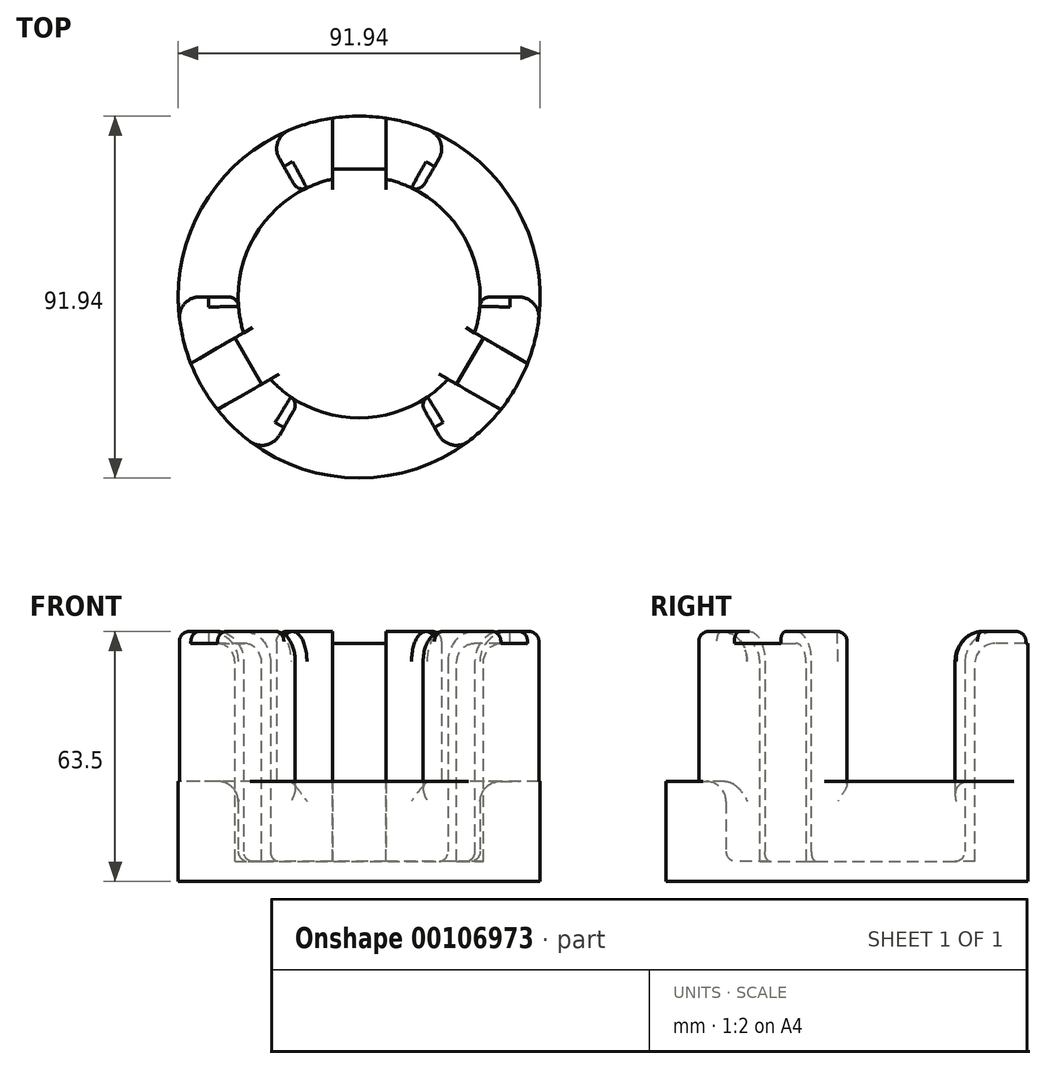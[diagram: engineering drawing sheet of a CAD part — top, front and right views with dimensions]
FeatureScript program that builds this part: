
annotation { "Feature Type Name" : "Feature", "Feature Type Description" : "" }
export const myFeature = defineFeature(function(context is Context, id is Id, definition is map)
    precondition{}
    {
        {
            var Q0;
            Q0=qCreatedBy(makeId("Front.planeOp"),FACE);
            var sketch = newSketch(context, id + "F0", { "sketchPlane" : qUnion([Q0])});
            skLineSegment(sketch, "E0", {"start": v(0, 0) * mm, "end": v(45.97, 0) * mm});
            skLineSegment(sketch, "E1", {"start": v(45.97, 0) * mm, "end": v(45.97, 63.5) * mm});
            skLineSegment(sketch, "E2", {"start": v(45.97, 63.5) * mm, "end": v(38.35, 63.5) * mm});
            skLineSegment(sketch, "E3", {"start": v(30.73, 55.88) * mm, "end": v(30.73, 5.08) * mm});
            skLineSegment(sketch, "E4", {"start": v(30.73, 5.08) * mm, "end": v(0, 5.08) * mm});
            skLineSegment(sketch, "E5", {"start": v(0, 5.08) * mm, "end": v(0, 0) * mm});
            skPoint(sketch, "E6.visualSharp", {"position": v(30.73, 63.5) * mm});
            skArc(sketch, "E6.filletArc", {"start": v(38.35, 63.5) * mm, "mid": v(32.97, 61.27) * mm, "end": v(30.73, 55.88) * mm});
            skLineSegment(sketch, "E7", {"start": v(0, 0) * mm, "end": v(0, 66.33) * mm, "construction": true});
            skSolve(sketch);
        }
        {
            var Q0;
            Q0=makeQuery(id+"F0.imprint","IMPRINT",FACE,{"disambiguationData":[TD([[makeQuery(id+"F0.imprint","IMPRINT",EDGE,{"derivedFrom":sQuery(id+"F0.wireOp",EDGE,"E0")}),1.0]])]});
            var Q1;
            Q1=sQuery(id+"F0.wireOp",EDGE,"E7");
            revolve(context, id + "F1", {"entities" : qUnion([Q0]), "axis" : qUnion([Q1]), "revolveType" : RevolveType.FULL});
        }
        {
            var Q0;
            Q0=makeQuery(id+"F1.opRevolve","SWEPT_FACE",FACE,{"disambiguationData":[OSD([sQuery(id+"F0.wireOp",EDGE,"E2")])]});
            var sketch = newSketch(context, id + "F2", { "sketchPlane" : qUnion([Q0])});
            skLineSegment(sketch, "E8.bottom", {"start": v(6.8, 32.51) * mm, "end": v(-6.8, 32.51) * mm});
            skLineSegment(sketch, "E8.top", {"start": v(6.8, 28.96) * mm, "end": v(-6.8, 28.96) * mm});
            skLineSegment(sketch, "E8.left", {"start": v(6.8, 32.51) * mm, "end": v(6.8, 28.96) * mm});
            skLineSegment(sketch, "E8.right", {"start": v(-6.8, 32.51) * mm, "end": v(-6.8, 28.96) * mm});
            skPoint(sketch, "E8.middle", {"position": v(0, 30.73) * mm});
            skLineSegment(sketch, "E9.1.0", {"start": v(-31.55, -10.37) * mm, "end": v(-28.47, -8.6) * mm});
            skLineSegment(sketch, "E9.1.1", {"start": v(-28.47, -8.6) * mm, "end": v(-21.68, -20.36) * mm});
            skLineSegment(sketch, "E9.1.2", {"start": v(-24.76, -22.14) * mm, "end": v(-21.68, -20.36) * mm});
            skLineSegment(sketch, "E9.1.3", {"start": v(-31.55, -10.37) * mm, "end": v(-24.76, -22.14) * mm});
            skLineSegment(sketch, "E9.2.0", {"start": v(24.76, -22.14) * mm, "end": v(21.68, -20.36) * mm});
            skLineSegment(sketch, "E9.2.1", {"start": v(21.68, -20.36) * mm, "end": v(28.47, -8.6) * mm});
            skLineSegment(sketch, "E9.2.2", {"start": v(31.55, -10.37) * mm, "end": v(28.47, -8.6) * mm});
            skLineSegment(sketch, "E9.2.3", {"start": v(24.76, -22.14) * mm, "end": v(31.55, -10.37) * mm});
            skPoint(sketch, "E9.center", {"position": v(0, 0) * mm});
            skSolve(sketch);
        }
        {
            var Q0;
            Q0 = qSketchRegion(id + "F2", true);
            extrude(context, id + "F3", {"entities" : qUnion([Q0]), "operationType" : NewBodyOperationType.REMOVE, "oppositeDirection" : true, "depth" : 58.42 * mm});
        }
        {
            var Q0;
            Q0=makeQuery(id+"F1.opRevolve","SWEPT_FACE",FACE,{"disambiguationData":[OSD([sQuery(id+"F0.wireOp",EDGE,"E2")])]});
            var sketch = newSketch(context, id + "F4", { "sketchPlane" : qUnion([Q0])});
            skLineSegment(sketch, "E10.bottom", {"start": v(-6.8, 52.9) * mm, "end": v(6.8, 52.9) * mm});
            skLineSegment(sketch, "E10.top", {"start": v(-6.8, 28.96) * mm, "end": v(6.8, 28.96) * mm});
            skLineSegment(sketch, "E10.left", {"start": v(-6.8, 52.9) * mm, "end": v(-6.8, 28.96) * mm});
            skLineSegment(sketch, "E10.right", {"start": v(6.8, 52.9) * mm, "end": v(6.8, 28.96) * mm});
            skLineSegment(sketch, "E11.1.0", {"start": v(-42.41, -32.33) * mm, "end": v(-49.2, -20.57) * mm});
            skLineSegment(sketch, "E11.1.1", {"start": v(-42.41, -32.33) * mm, "end": v(-21.68, -20.36) * mm});
            skLineSegment(sketch, "E11.1.2", {"start": v(-49.2, -20.57) * mm, "end": v(-28.47, -8.6) * mm});
            skLineSegment(sketch, "E11.1.3", {"start": v(-21.68, -20.36) * mm, "end": v(-28.47, -8.6) * mm});
            skLineSegment(sketch, "E11.2.0", {"start": v(49.2, -20.57) * mm, "end": v(42.41, -32.33) * mm});
            skLineSegment(sketch, "E11.2.1", {"start": v(49.2, -20.57) * mm, "end": v(28.47, -8.6) * mm});
            skLineSegment(sketch, "E11.2.2", {"start": v(42.41, -32.33) * mm, "end": v(21.68, -20.36) * mm});
            skLineSegment(sketch, "E11.2.3", {"start": v(28.47, -8.6) * mm, "end": v(21.68, -20.36) * mm});
            skPoint(sketch, "E11.center", {"position": v(0, 0) * mm});
            skSolve(sketch);
        }
        {
            var Q0;
            Q0 = qSketchRegion(id + "F4", true);
            extrude(context, id + "F5", {"entities" : qUnion([Q0]), "operationType" : NewBodyOperationType.REMOVE, "oppositeDirection" : true, "depth" : 3.05 * mm});
        }
        {
            var Q0;
            Q0=makeQuery(id+"F5.boolean.opBoolean","INTERSECT",EDGE,{"derivedFrom":[makeQuery(id+"F3.boolean.opBoolean","COPY",FACE,{"derivedFrom":makeQuery(id+"F3.opExtrude","SWEPT_FACE",FACE,{"disambiguationData":[OSD([sQuery(id+"F2.wireOp",EDGE,"E9.1.3")])]})}),makeQuery(id+"F5.opExtrude","CAP_FACE",FACE,{"disambiguationData":[OSD([sQuery(id+"F4.wireOp",EDGE,"E11.1.0"),sQuery(id+"F4.wireOp",EDGE,"E11.1.1"),sQuery(id+"F4.wireOp",EDGE,"E11.1.2"),sQuery(id+"F4.wireOp",EDGE,"E11.1.3")])],"isStart":false})]});
            var Q1;
            Q1=makeQuery(id+"F5.boolean.opBoolean","INTERSECT",EDGE,{"derivedFrom":[makeQuery(id+"F3.boolean.opBoolean","COPY",FACE,{"derivedFrom":makeQuery(id+"F3.opExtrude","SWEPT_FACE",FACE,{"disambiguationData":[OSD([sQuery(id+"F2.wireOp",EDGE,"E8.bottom")])]})}),makeQuery(id+"F5.opExtrude","CAP_FACE",FACE,{"disambiguationData":[OSD([sQuery(id+"F4.wireOp",EDGE,"E10.bottom"),sQuery(id+"F4.wireOp",EDGE,"E10.top"),sQuery(id+"F4.wireOp",EDGE,"E10.left"),sQuery(id+"F4.wireOp",EDGE,"E10.right")])],"isStart":false})]});
            var Q2;
            Q2=makeQuery(id+"F5.boolean.opBoolean","INTERSECT",EDGE,{"derivedFrom":[makeQuery(id+"F3.boolean.opBoolean","COPY",FACE,{"derivedFrom":makeQuery(id+"F3.opExtrude","SWEPT_FACE",FACE,{"disambiguationData":[OSD([sQuery(id+"F2.wireOp",EDGE,"E9.2.3")])]})}),makeQuery(id+"F5.opExtrude","CAP_FACE",FACE,{"disambiguationData":[OSD([sQuery(id+"F4.wireOp",EDGE,"E11.2.0"),sQuery(id+"F4.wireOp",EDGE,"E11.2.1"),sQuery(id+"F4.wireOp",EDGE,"E11.2.2"),sQuery(id+"F4.wireOp",EDGE,"E11.2.3")])],"isStart":false})]});
            fillet(context, id + "F6", {"entities" : qUnion([Q0, Q1, Q2]), "radius" : 5.08 * mm, "tangentPropagation" : true, "allowEdgeOverflow" : false});
        }
        {
            var Q0;
            {var subQ0=sQuery(id+"F0.wireOp",EDGE,"E2");Q0=makeQuery(id+"F2.imprint","IMPRINT",FACE,{"disambiguationData":[TD([[makeQuery(id+"F2.imprint","IMPRINT",EDGE,{"derivedFrom":makeQuery(id+"F1.opRevolve","SWEPT_EDGE",EDGE,{"disambiguationData":[OSD([sQuery(id+"F0.wireOp",EDGE,"E1"),subQ0])]})}),-1.0]])]});}
            var sketch = newSketch(context, id + "F7", { "sketchPlane" : qUnion([Q0])});
            skLineSegment(sketch, "E12", {"start": v(0, 0) * mm, "end": v(-29.33, -50.8) * mm});
            skLineSegment(sketch, "E13", {"start": v(-29.33, -50.8) * mm, "end": v(0, -50.8) * mm});
            skLineSegment(sketch, "E14", {"start": v(0, -50.8) * mm, "end": v(0, 0) * mm});
            skLineSegment(sketch, "E15.MirrorCS", {"start": v(0, 0) * mm, "end": v(29.33, -50.8) * mm});
            skLineSegment(sketch, "E16.MirrorCS", {"start": v(29.33, -50.8) * mm, "end": v(0, -50.8) * mm});
            skLineSegment(sketch, "E17.1.0", {"start": v(0, 0) * mm, "end": v(58.66, 0) * mm});
            skLineSegment(sketch, "E17.1.1", {"start": v(0, 0) * mm, "end": v(29.33, 50.8) * mm});
            skLineSegment(sketch, "E17.1.2", {"start": v(29.33, 50.8) * mm, "end": v(44, 25.4) * mm});
            skLineSegment(sketch, "E17.2.0", {"start": v(0, 0) * mm, "end": v(-29.33, 50.8) * mm});
            skLineSegment(sketch, "E17.2.1", {"start": v(0, 0) * mm, "end": v(-58.66, 0) * mm});
            skLineSegment(sketch, "E17.2.2", {"start": v(-58.66, 0) * mm, "end": v(-44, 25.4) * mm});
            skPoint(sketch, "E17.center", {"position": v(0, 0) * mm});
            skLineSegment(sketch, "E18.1.1", {"start": v(58.66, 0) * mm, "end": v(44, 25.4) * mm});
            skLineSegment(sketch, "E18.2.1", {"start": v(-29.33, 50.8) * mm, "end": v(-44, 25.4) * mm});
            skSolve(sketch);
        }
        {
            var Q0;
            Q0 = qSketchRegion(id + "F7", true);
            extrude(context, id + "F8", {"entities" : qUnion([Q0]), "operationType" : NewBodyOperationType.REMOVE, "oppositeDirection" : true, "depth" : 38.1 * mm});
        }
        {
            var Q0;
            {var subQ0=sQuery(id+"F2.wireOp",EDGE,"E9.1.2");Q0=makeQuery(id+"F8.boolean.opBoolean","INTERSECT",EDGE,{"derivedFrom":[makeQuery(id+"F3.boolean.opBoolean","SPLIT",FACE,{"disambiguationData":[TD([makeQuery(id+"F3.opExtrude","SWEPT_FACE",FACE,{"disambiguationData":[OSD([subQ0])]})])],"derivedFrom":makeQuery(id+"F1.opRevolve","SWEPT_FACE",FACE,{"disambiguationData":[OSD([sQuery(id+"F0.wireOp",EDGE,"E3")])]})}),makeQuery(id+"F8.opExtrude","CAP_FACE",FACE,{"disambiguationData":[OSD([sQuery(id+"F7.wireOp",EDGE,"E12"),sQuery(id+"F7.wireOp",EDGE,"E13"),sQuery(id+"F7.wireOp",EDGE,"E15.MirrorCS"),sQuery(id+"F7.wireOp",EDGE,"E16.MirrorCS")])],"isStart":false})]});}
            var Q1;
            {var subQ0=sQuery(id+"F2.wireOp",EDGE,"E8.right");Q1=makeQuery(id+"F8.boolean.opBoolean","INTERSECT",EDGE,{"derivedFrom":[makeQuery(id+"F3.boolean.opBoolean","SPLIT",FACE,{"disambiguationData":[TD([makeQuery(id+"F3.opExtrude","SWEPT_FACE",FACE,{"disambiguationData":[OSD([subQ0])]})])],"derivedFrom":makeQuery(id+"F1.opRevolve","SWEPT_FACE",FACE,{"disambiguationData":[OSD([sQuery(id+"F0.wireOp",EDGE,"E3")])]})}),makeQuery(id+"F8.opExtrude","CAP_FACE",FACE,{"disambiguationData":[OSD([sQuery(id+"F7.wireOp",EDGE,"E17.2.0"),sQuery(id+"F7.wireOp",EDGE,"E17.2.1"),sQuery(id+"F7.wireOp",EDGE,"E17.2.2"),sQuery(id+"F7.wireOp",EDGE,"E18.2.1")])],"isStart":false})]});}
            var Q2;
            {var subQ0=sQuery(id+"F2.wireOp",EDGE,"E8.left");Q2=makeQuery(id+"F8.boolean.opBoolean","INTERSECT",EDGE,{"derivedFrom":[makeQuery(id+"F3.boolean.opBoolean","SPLIT",FACE,{"disambiguationData":[TD([makeQuery(id+"F3.opExtrude","SWEPT_FACE",FACE,{"disambiguationData":[OSD([subQ0])]})])],"derivedFrom":makeQuery(id+"F1.opRevolve","SWEPT_FACE",FACE,{"disambiguationData":[OSD([sQuery(id+"F0.wireOp",EDGE,"E3")])]})}),makeQuery(id+"F8.opExtrude","CAP_FACE",FACE,{"disambiguationData":[OSD([sQuery(id+"F7.wireOp",EDGE,"E17.1.0"),sQuery(id+"F7.wireOp",EDGE,"E17.1.1"),sQuery(id+"F7.wireOp",EDGE,"E17.1.2"),sQuery(id+"F7.wireOp",EDGE,"E18.1.1")])],"isStart":false})]});}
            var Q3;
            Q3=makeQuery(id+"F8.boolean.opBoolean","INTERSECT",EDGE,{"derivedFrom":[makeQuery(id+"F1.opRevolve","SWEPT_FACE",FACE,{"disambiguationData":[OSD([sQuery(id+"F0.wireOp",EDGE,"E1")])]}),makeQuery(id+"F8.opExtrude","SWEPT_FACE",FACE,{"disambiguationData":[OSD([sQuery(id+"F7.wireOp",EDGE,"E17.1.0")])]})]});
            var Q4;
            Q4=makeQuery(id+"F8.boolean.opBoolean","INTERSECT",EDGE,{"derivedFrom":[makeQuery(id+"F1.opRevolve","SWEPT_FACE",FACE,{"disambiguationData":[OSD([sQuery(id+"F0.wireOp",EDGE,"E1")])]}),makeQuery(id+"F8.opExtrude","SWEPT_FACE",FACE,{"disambiguationData":[OSD([sQuery(id+"F7.wireOp",EDGE,"E17.1.1")])]})]});
            var Q5;
            Q5=makeQuery(id+"F8.boolean.opBoolean","INTERSECT",EDGE,{"derivedFrom":[makeQuery(id+"F1.opRevolve","SWEPT_FACE",FACE,{"disambiguationData":[OSD([sQuery(id+"F0.wireOp",EDGE,"E1")])]}),makeQuery(id+"F8.opExtrude","SWEPT_FACE",FACE,{"disambiguationData":[OSD([sQuery(id+"F7.wireOp",EDGE,"E17.2.0")])]})]});
            var Q6;
            Q6=makeQuery(id+"F8.boolean.opBoolean","INTERSECT",EDGE,{"derivedFrom":[makeQuery(id+"F1.opRevolve","SWEPT_FACE",FACE,{"disambiguationData":[OSD([sQuery(id+"F0.wireOp",EDGE,"E1")])]}),makeQuery(id+"F8.opExtrude","SWEPT_FACE",FACE,{"disambiguationData":[OSD([sQuery(id+"F7.wireOp",EDGE,"E17.2.1")])]})]});
            var Q7;
            Q7=makeQuery(id+"F8.boolean.opBoolean","INTERSECT",EDGE,{"derivedFrom":[makeQuery(id+"F1.opRevolve","SWEPT_FACE",FACE,{"disambiguationData":[OSD([sQuery(id+"F0.wireOp",EDGE,"E1")])]}),makeQuery(id+"F8.opExtrude","SWEPT_FACE",FACE,{"disambiguationData":[OSD([sQuery(id+"F7.wireOp",EDGE,"E12")])]})]});
            var Q8;
            Q8=makeQuery(id+"F8.boolean.opBoolean","INTERSECT",EDGE,{"derivedFrom":[makeQuery(id+"F1.opRevolve","SWEPT_FACE",FACE,{"disambiguationData":[OSD([sQuery(id+"F0.wireOp",EDGE,"E1")])]}),makeQuery(id+"F8.opExtrude","SWEPT_FACE",FACE,{"disambiguationData":[OSD([sQuery(id+"F7.wireOp",EDGE,"E15.MirrorCS")])]})]});
            fillet(context, id + "F9", {"entities" : qUnion([Q0, Q1, Q2, Q3, Q4, Q5, Q6, Q7, Q8]), "radius" : 5.08 * mm, "tangentPropagation" : true, "allowEdgeOverflow" : false});
        }
        {
            var Q0;
            {var subQ0=sQuery(id+"F2.wireOp",EDGE,"E9.1.2");var subQ2=sQuery(id+"F0.wireOp",EDGE,"E4");var subQ3=sQuery(id+"F0.wireOp",EDGE,"E3");Q0=makeQuery(id+"F3.boolean.opBoolean","SPLIT",EDGE,{"disambiguationData":[TD([makeQuery(id+"F3.opExtrude","SWEPT_FACE",FACE,{"disambiguationData":[OSD([subQ0])]})])],"derivedFrom":makeQuery(id+"F1.opRevolve","SWEPT_EDGE",EDGE,{"disambiguationData":[OSD([subQ3,subQ2])]})});}
            var Q1;
            {var subQ0=sQuery(id+"F2.wireOp",EDGE,"E8.right");var subQ1=sQuery(id+"F0.wireOp",EDGE,"E4");var subQ2=sQuery(id+"F0.wireOp",EDGE,"E3");Q1=makeQuery(id+"F3.boolean.opBoolean","SPLIT",EDGE,{"disambiguationData":[TD([makeQuery(id+"F3.opExtrude","SWEPT_FACE",FACE,{"disambiguationData":[OSD([subQ0])]})])],"derivedFrom":makeQuery(id+"F1.opRevolve","SWEPT_EDGE",EDGE,{"disambiguationData":[OSD([subQ2,subQ1])]})});}
            var Q2;
            {var subQ0=sQuery(id+"F2.wireOp",EDGE,"E8.left");var subQ1=sQuery(id+"F0.wireOp",EDGE,"E4");var subQ2=sQuery(id+"F0.wireOp",EDGE,"E3");Q2=makeQuery(id+"F3.boolean.opBoolean","SPLIT",EDGE,{"disambiguationData":[TD([makeQuery(id+"F3.opExtrude","SWEPT_FACE",FACE,{"disambiguationData":[OSD([subQ0])]})])],"derivedFrom":makeQuery(id+"F1.opRevolve","SWEPT_EDGE",EDGE,{"disambiguationData":[OSD([subQ2,subQ1])]})});}
            fillet(context, id + "F10", {"entities" : qUnion([Q0, Q1, Q2]), "radius" : 2.54 * mm, "tangentPropagation" : true, "allowEdgeOverflow" : false});
        }
        {
            var Q0;
            {var subQ0=sQuery(id+"F2.wireOp",EDGE,"E9.1.2");Q0=makeQuery(id+"F8.boolean.opBoolean","INTERSECT",EDGE,{"derivedFrom":[makeQuery(id+"F3.boolean.opBoolean","SPLIT",FACE,{"disambiguationData":[TD([makeQuery(id+"F3.opExtrude","SWEPT_FACE",FACE,{"disambiguationData":[OSD([subQ0])]})])],"derivedFrom":makeQuery(id+"F1.opRevolve","SWEPT_FACE",FACE,{"disambiguationData":[OSD([sQuery(id+"F0.wireOp",EDGE,"E3")])]})}),makeQuery(id+"F8.opExtrude","SWEPT_FACE",FACE,{"disambiguationData":[OSD([sQuery(id+"F7.wireOp",EDGE,"E12")])]})]});}
            var Q1;
            {var subQ0=sQuery(id+"F2.wireOp",EDGE,"E8.right");Q1=makeQuery(id+"F8.boolean.opBoolean","INTERSECT",EDGE,{"derivedFrom":[makeQuery(id+"F3.boolean.opBoolean","SPLIT",FACE,{"disambiguationData":[TD([makeQuery(id+"F3.opExtrude","SWEPT_FACE",FACE,{"disambiguationData":[OSD([subQ0])]})])],"derivedFrom":makeQuery(id+"F1.opRevolve","SWEPT_FACE",FACE,{"disambiguationData":[OSD([sQuery(id+"F0.wireOp",EDGE,"E3")])]})}),makeQuery(id+"F8.opExtrude","SWEPT_FACE",FACE,{"disambiguationData":[OSD([sQuery(id+"F7.wireOp",EDGE,"E17.2.1")])]})]});}
            var Q2;
            {var subQ0=sQuery(id+"F2.wireOp",EDGE,"E8.right");Q2=makeQuery(id+"F8.boolean.opBoolean","INTERSECT",EDGE,{"derivedFrom":[makeQuery(id+"F3.boolean.opBoolean","SPLIT",FACE,{"disambiguationData":[TD([makeQuery(id+"F3.opExtrude","SWEPT_FACE",FACE,{"disambiguationData":[OSD([subQ0])]})])],"derivedFrom":makeQuery(id+"F1.opRevolve","SWEPT_FACE",FACE,{"disambiguationData":[OSD([sQuery(id+"F0.wireOp",EDGE,"E3")])]})}),makeQuery(id+"F8.opExtrude","SWEPT_FACE",FACE,{"disambiguationData":[OSD([sQuery(id+"F7.wireOp",EDGE,"E17.2.0")])]})]});}
            var Q3;
            {var subQ0=sQuery(id+"F2.wireOp",EDGE,"E8.left");Q3=makeQuery(id+"F8.boolean.opBoolean","INTERSECT",EDGE,{"derivedFrom":[makeQuery(id+"F3.boolean.opBoolean","SPLIT",FACE,{"disambiguationData":[TD([makeQuery(id+"F3.opExtrude","SWEPT_FACE",FACE,{"disambiguationData":[OSD([subQ0])]})])],"derivedFrom":makeQuery(id+"F1.opRevolve","SWEPT_FACE",FACE,{"disambiguationData":[OSD([sQuery(id+"F0.wireOp",EDGE,"E3")])]})}),makeQuery(id+"F8.opExtrude","SWEPT_FACE",FACE,{"disambiguationData":[OSD([sQuery(id+"F7.wireOp",EDGE,"E17.1.1")])]})]});}
            var Q4;
            {var subQ0=sQuery(id+"F2.wireOp",EDGE,"E8.left");Q4=makeQuery(id+"F8.boolean.opBoolean","INTERSECT",EDGE,{"derivedFrom":[makeQuery(id+"F3.boolean.opBoolean","SPLIT",FACE,{"disambiguationData":[TD([makeQuery(id+"F3.opExtrude","SWEPT_FACE",FACE,{"disambiguationData":[OSD([subQ0])]})])],"derivedFrom":makeQuery(id+"F1.opRevolve","SWEPT_FACE",FACE,{"disambiguationData":[OSD([sQuery(id+"F0.wireOp",EDGE,"E3")])]})}),makeQuery(id+"F8.opExtrude","SWEPT_FACE",FACE,{"disambiguationData":[OSD([sQuery(id+"F7.wireOp",EDGE,"E17.1.0")])]})]});}
            var Q5;
            {var subQ0=sQuery(id+"F2.wireOp",EDGE,"E9.1.2");Q5=makeQuery(id+"F8.boolean.opBoolean","INTERSECT",EDGE,{"derivedFrom":[makeQuery(id+"F3.boolean.opBoolean","SPLIT",FACE,{"disambiguationData":[TD([makeQuery(id+"F3.opExtrude","SWEPT_FACE",FACE,{"disambiguationData":[OSD([subQ0])]})])],"derivedFrom":makeQuery(id+"F1.opRevolve","SWEPT_FACE",FACE,{"disambiguationData":[OSD([sQuery(id+"F0.wireOp",EDGE,"E3")])]})}),makeQuery(id+"F8.opExtrude","SWEPT_FACE",FACE,{"disambiguationData":[OSD([sQuery(id+"F7.wireOp",EDGE,"E15.MirrorCS")])]})]});}
            fillet(context, id + "F11", {"entities" : qUnion([Q0, Q1, Q2, Q3, Q4, Q5]), "radius" : 2.54 * mm, "tangentPropagation" : true, "allowEdgeOverflow" : false});
        }
    });
